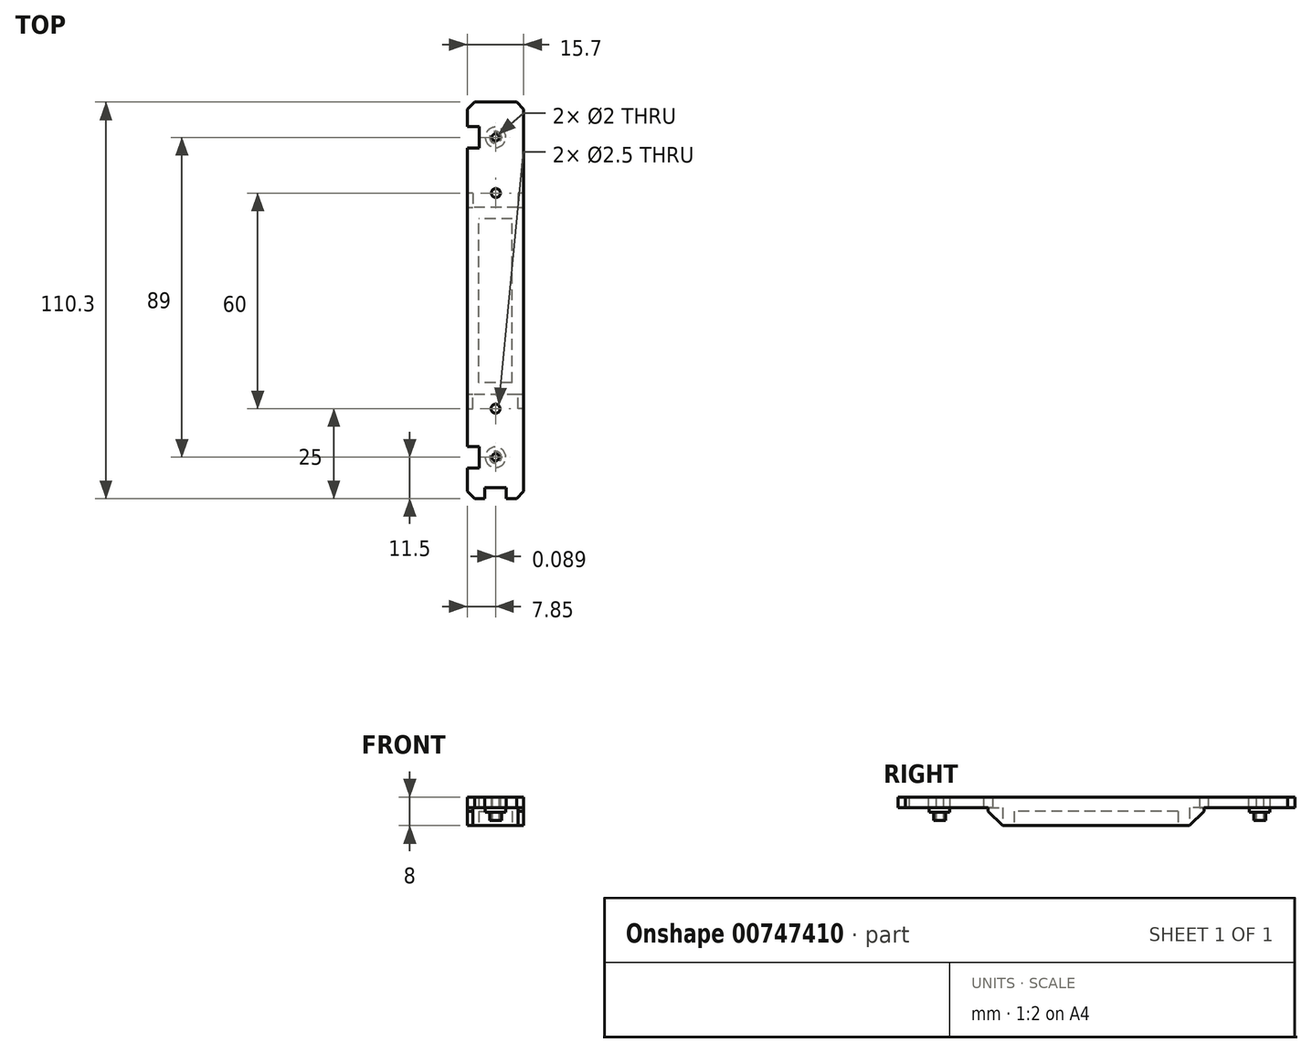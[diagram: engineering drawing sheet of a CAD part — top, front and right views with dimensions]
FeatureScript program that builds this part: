
annotation { "Feature Type Name" : "Feature", "Feature Type Description" : "" }
export const myFeature = defineFeature(function(context is Context, id is Id, definition is map)
    precondition{}
    {
        {
            var Q0;
            Q0=qCreatedBy(makeId("Right.planeOp"),FACE);
            var sketch = newSketch(context, id + "F0", { "sketchPlane" : qUnion([Q0])});
            skLineSegment(sketch, "E0", {"start": v(-25, 5) * mm, "end": v(0, 5) * mm});
            skLineSegment(sketch, "E1", {"start": v(0, 5) * mm, "end": v(0, 0) * mm});
            skLineSegment(sketch, "E2", {"start": v(60, 0) * mm, "end": v(60, 5) * mm});
            skLineSegment(sketch, "E3", {"start": v(60, 5) * mm, "end": v(85.3, 5) * mm});
            skLineSegment(sketch, "E4", {"start": v(85.3, 5) * mm, "end": v(85.3, 8) * mm});
            skLineSegment(sketch, "E5", {"start": v(-25, 8) * mm, "end": v(-25, 5) * mm});
            skLineSegment(sketch, "E6.trimOffspring", {"start": v(85.3, 8) * mm, "end": v(-25, 8) * mm});
            skLineSegment(sketch, "E7", {"start": v(0, 0) * mm, "end": v(0, 0) * mm});
            skLineSegment(sketch, "E8", {"start": v(0, 0) * mm, "end": v(60, 0) * mm});
            skSolve(sketch);
        }
        {
            var Q0;
            Q0 = qSketchRegion(id + "F0", true);
            extrude(context, id + "F1", {"entities" : qUnion([Q0]), "depth" : 15.7 * mm, "offsetDistance" : 25 * mm, "symmetric" : true});
        }
        {
            var Q0;
            Q0=makeQuery(id+"F1.opExtrude","CAP_EDGE",EDGE,{"disambiguationData":[OSD([sQuery(id+"F0.wireOp",EDGE,"E5")])],"isStart":false});
            var Q1;
            Q1=makeQuery(id+"F1.opExtrude","CAP_EDGE",EDGE,{"disambiguationData":[OSD([sQuery(id+"F0.wireOp",EDGE,"E5")])],"isStart":true});
            var Q2;
            Q2=makeQuery(id+"F1.opExtrude","CAP_EDGE",EDGE,{"disambiguationData":[OSD([sQuery(id+"F0.wireOp",EDGE,"E4")])],"isStart":false});
            var Q3;
            Q3=makeQuery(id+"F1.opExtrude","CAP_EDGE",EDGE,{"disambiguationData":[OSD([sQuery(id+"F0.wireOp",EDGE,"E4")])],"isStart":true});
            chamfer(context, id + "F2", {"entities" : qUnion([Q0, Q1, Q2, Q3]), "width" : 2 * mm, "tangentPropagation" : true});
        }
        {
            var Q0;
            Q0=makeQuery(id+"F1.opExtrude","SWEPT_FACE",FACE,{"disambiguationData":[OSD([sQuery(id+"F0.wireOp",EDGE,"E0")])]});
            var sketch = newSketch(context, id + "F3", { "sketchPlane" : qUnion([Q0])});
            skCircle(sketch, "E9", {"center": v(0, 13.5) * mm, "radius": 1 * mm});
            skCircle(sketch, "E10", {"center": v(0, -75.5) * mm, "radius": 1 * mm});
            skLineSegment(sketch, "E11", {"start": v(0, 13.5) * mm, "end": v(0, 0) * mm, "construction": true});
            skLineSegment(sketch, "E12", {"start": v(0, 0) * mm, "end": v(0, -75.5) * mm, "construction": true});
            skSolve(sketch);
        }
        {
            var Q0;
            Q0 = qSketchRegion(id + "F3", true);
            extrude(context, id + "F4", {"entities" : qUnion([Q0]), "operationType" : NewBodyOperationType.REMOVE, "endBound" : BoundingType.UP_TO_NEXT, "oppositeDirection" : true, "depth" : 25 * mm, "offsetDistance" : 25 * mm});
        }
        {
            var Q0;
            Q0=makeQuery(id+"F1.opExtrude","SWEPT_FACE",FACE,{"disambiguationData":[OSD([sQuery(id+"F0.wireOp",EDGE,"E7"),sQuery(id+"F0.wireOp",EDGE,"E8")])]});
            var sketch = newSketch(context, id + "F5", { "sketchPlane" : qUnion([Q0])});
            skLineSegment(sketch, "E13.bottom", {"start": v(6.25, 0) * mm, "end": v(-6.25, 0) * mm});
            skLineSegment(sketch, "E13.top", {"start": v(6.25, -4) * mm, "end": v(-6.25, -4) * mm});
            skLineSegment(sketch, "E13.left", {"start": v(6.25, 0) * mm, "end": v(6.25, -4) * mm});
            skLineSegment(sketch, "E13.right", {"start": v(-6.25, 0) * mm, "end": v(-6.25, -4) * mm});
            skLineSegment(sketch, "E14", {"start": v(0, -4) * mm, "end": v(0, 0) * mm, "construction": true});
            skPoint(sketch, "E14.startSnap0", {"position": v(0, -4) * mm});
            skLineSegment(sketch, "E15.bottom", {"start": v(6.25, -60) * mm, "end": v(-6.25, -60) * mm});
            skLineSegment(sketch, "E15.top", {"start": v(6.25, -56) * mm, "end": v(-6.25, -56) * mm});
            skLineSegment(sketch, "E15.left", {"start": v(6.25, -60) * mm, "end": v(6.25, -56) * mm});
            skLineSegment(sketch, "E15.right", {"start": v(-6.25, -60) * mm, "end": v(-6.25, -56) * mm});
            skSolve(sketch);
        }
        {
            var Q0;
            Q0 = qSketchRegion(id + "F5", true);
            var Q1;
            Q1=makeQuery(id+"F1.opExtrude","SWEPT_FACE",FACE,{"disambiguationData":[OSD([sQuery(id+"F0.wireOp",EDGE,"E0")])]});
            extrude(context, id + "F6", {"entities" : qUnion([Q0]), "operationType" : NewBodyOperationType.REMOVE, "endBound" : BoundingType.UP_TO_SURFACE, "oppositeDirection" : true, "depth" : 25 * mm, "endBoundEntityFace" : qUnion([Q1]), "offsetDistance" : 25 * mm});
        }
        {
            var Q0;
            {Q0=qUnion([makeQuery(id+"F6.boolean.opBoolean","MERGE",FACE,{"derivedFrom":[makeQuery(id+"F1.opExtrude","SWEPT_FACE",FACE,{"disambiguationData":[OSD([sQuery(id+"F0.wireOp",EDGE,"E0")])]})],"fromTools":[makeQuery(id+"F6.opExtrude","CAP_FACE",FACE,{"disambiguationData":[OSD([sQuery(id+"F5.wireOp",EDGE,"QtaLUQ9K-xFjA-aVn2-jr8E-2nqdviAdBmNi"),sQuery(id+"F5.wireOp",EDGE,"MIOGkYBv-3kq0-NffD-4QcD-ZkNMdwIdXdjM"),sQuery(id+"F5.wireOp",EDGE,"2ayCmlRU-f8e1-FQng-G2dl-z1bR76XOkfuW"),sQuery(id+"F5.wireOp",EDGE,"Q6Nk2F50-RIht-aVqs-q8m5-kIFtcKPUQnbz")])],"isStart":false})]}),makeQuery(id+"F6.boolean.opBoolean","MERGE",FACE,{"derivedFrom":[makeQuery(id+"F1.opExtrude","SWEPT_FACE",FACE,{"disambiguationData":[OSD([sQuery(id+"F0.wireOp",EDGE,"E3")])]})],"fromTools":[makeQuery(id+"F6.opExtrude","CAP_FACE",FACE,{"disambiguationData":[OSD([sQuery(id+"F5.wireOp",EDGE,"UIq0axqO-XxSW-t0FF-EL4X-YCJ9C5suXqDZ"),sQuery(id+"F5.wireOp",EDGE,"48w0VJL2-kqmk-4goN-fqhj-BqvBEsziLtPm"),sQuery(id+"F5.wireOp",EDGE,"iuIQCKwA-ER4D-4RKV-h3Pt-EvZXLoRTW6qv"),sQuery(id+"F5.wireOp",EDGE,"zWaE9cvL-vTQC-7oDd-e5Ol-owMjjvXLEkyw")])],"isStart":false})]})]);}
            var sketch = newSketch(context, id + "F7", { "sketchPlane" : qUnion([Q0])});
            skCircle(sketch, "E16", {"center": v(0, 0) * mm, "radius": 1.25 * mm});
            skCircle(sketch, "E17", {"center": v(0.09, -60) * mm, "radius": 1.25 * mm});
            skLineSegment(sketch, "E18", {"start": v(0, -4) * mm, "end": v(0, 0) * mm, "construction": true});
            skLineSegment(sketch, "E19", {"start": v(0.09, -60) * mm, "end": v(0, -56) * mm, "construction": true});
            skSolve(sketch);
        }
        {
            var Q0;
            Q0 = qSketchRegion(id + "F7", true);
            extrude(context, id + "F8", {"entities" : qUnion([Q0]), "operationType" : NewBodyOperationType.REMOVE, "endBound" : BoundingType.UP_TO_NEXT, "oppositeDirection" : true, "depth" : 25 * mm, "offsetDistance" : 25 * mm});
        }
        {
            var Q0;
            Q0=makeQuery(id+"F6.boolean.opBoolean","MERGE",FACE,{"derivedFrom":[makeQuery(id+"F1.opExtrude","SWEPT_FACE",FACE,{"disambiguationData":[OSD([sQuery(id+"F0.wireOp",EDGE,"E3")])]})],"fromTools":[makeQuery(id+"F6.opExtrude","CAP_FACE",FACE,{"disambiguationData":[OSD([sQuery(id+"F5.wireOp",EDGE,"UIq0axqO-XxSW-t0FF-EL4X-YCJ9C5suXqDZ"),sQuery(id+"F5.wireOp",EDGE,"48w0VJL2-kqmk-4goN-fqhj-BqvBEsziLtPm"),sQuery(id+"F5.wireOp",EDGE,"iuIQCKwA-ER4D-4RKV-h3Pt-EvZXLoRTW6qv")])],"isStart":false})]});
            var sketch = newSketch(context, id + "F9", { "sketchPlane" : qUnion([Q0])});
            skCircle(sketch, "E20", {"center": v(0, -75.5) * mm, "radius": 1.65 * mm});
            skCircle(sketch, "E21", {"center": v(0, 13.5) * mm, "radius": 1.65 * mm});
            skCircle(sketch, "E22.0", {"center": v(0, -75.5) * mm, "radius": 1 * mm});
            skCircle(sketch, "E23.0", {"center": v(0, 13.5) * mm, "radius": 1 * mm});
            skSolve(sketch);
        }
        {
            var Q0;
            Q0 = qSketchRegion(id + "F9", true);
            extrude(context, id + "F10", {"entities" : qUnion([Q0]), "operationType" : NewBodyOperationType.ADD, "depth" : 3.5 * mm, "offsetDistance" : 25 * mm});
        }
        {
            var Q0;
            Q0=makeQuery(id+"F1.opExtrude","SWEPT_FACE",FACE,{"disambiguationData":[OSD([sQuery(id+"F0.wireOp",EDGE,"E6.trimOffspring")])]});
            var sketch = newSketch(context, id + "F11", { "sketchPlane" : qUnion([Q0])});
            skLineSegment(sketch, "E24", {"start": v(-7.85, -10.5) * mm, "end": v(-4.5, -10.5) * mm});
            skLineSegment(sketch, "E25", {"start": v(-4.5, -10.5) * mm, "end": v(-4.5, -16.5) * mm});
            skLineSegment(sketch, "E26", {"start": v(-4.5, -16.5) * mm, "end": v(-7.85, -16.5) * mm});
            skLineSegment(sketch, "E27", {"start": v(-7.85, -16.5) * mm, "end": v(-7.85, -10.5) * mm});
            skLineSegment(sketch, "E28", {"start": v(0, -13.5) * mm, "end": v(0, -7.98) * mm, "construction": true});
            skLineSegment(sketch, "E29", {"start": v(0, -13.5) * mm, "end": v(-4.5, -13.5) * mm, "construction": true});
            skLineSegment(sketch, "E30.bottom", {"start": v(-7.85, 72.5) * mm, "end": v(-4.5, 72.5) * mm});
            skLineSegment(sketch, "E30.top", {"start": v(-7.85, 78.5) * mm, "end": v(-4.5, 78.5) * mm});
            skLineSegment(sketch, "E30.left", {"start": v(-7.85, 72.5) * mm, "end": v(-7.85, 78.5) * mm});
            skLineSegment(sketch, "E30.right", {"start": v(-4.5, 72.5) * mm, "end": v(-4.5, 78.5) * mm});
            skLineSegment(sketch, "E31", {"start": v(-4.5, 75.5) * mm, "end": v(0, 75.5) * mm, "construction": true});
            skSolve(sketch);
        }
        {
            var Q0;
            Q0 = qSketchRegion(id + "F11", true);
            extrude(context, id + "F12", {"entities" : qUnion([Q0]), "operationType" : NewBodyOperationType.REMOVE, "endBound" : BoundingType.UP_TO_NEXT, "oppositeDirection" : true, "depth" : 25 * mm, "offsetDistance" : 25 * mm});
        }
        {
            var Q0;
            Q0=makeQuery(id+"F6.boolean.opBoolean","MERGE",FACE,{"derivedFrom":[makeQuery(id+"F1.opExtrude","SWEPT_FACE",FACE,{"disambiguationData":[OSD([sQuery(id+"F0.wireOp",EDGE,"E3")])]})],"fromTools":[makeQuery(id+"F6.opExtrude","CAP_FACE",FACE,{"disambiguationData":[OSD([sQuery(id+"F5.wireOp",EDGE,"UIq0axqO-XxSW-t0FF-EL4X-YCJ9C5suXqDZ"),sQuery(id+"F5.wireOp",EDGE,"48w0VJL2-kqmk-4goN-fqhj-BqvBEsziLtPm"),sQuery(id+"F5.wireOp",EDGE,"iuIQCKwA-ER4D-4RKV-h3Pt-EvZXLoRTW6qv")])],"isStart":false})]});
            var sketch = newSketch(context, id + "F13", { "sketchPlane" : qUnion([Q0])});
            skCircle(sketch, "E32", {"center": v(0, -75.5) * mm, "radius": 2.85 * mm});
            skCircle(sketch, "E33", {"center": v(0, 13.5) * mm, "radius": 2.85 * mm});
            skCircle(sketch, "E34.0", {"center": v(0, 13.5) * mm, "radius": 1 * mm});
            skCircle(sketch, "E34.1", {"center": v(0, -75.5) * mm, "radius": 1 * mm});
            skSolve(sketch);
        }
        {
            var Q0;
            Q0 = qSketchRegion(id + "F13", true);
            extrude(context, id + "F14", {"entities" : qUnion([Q0]), "operationType" : NewBodyOperationType.ADD, "depth" : 1.2 * mm, "offsetDistance" : 25 * mm});
        }
        {
            var Q0;
            Q0=makeQuery(id+"F6.boolean.opBoolean","MERGE",FACE,{"derivedFrom":[makeQuery(id+"F1.opExtrude","SWEPT_FACE",FACE,{"disambiguationData":[OSD([sQuery(id+"F0.wireOp",EDGE,"E0")])]})],"fromTools":[makeQuery(id+"F6.opExtrude","CAP_FACE",FACE,{"disambiguationData":[OSD([sQuery(id+"F5.wireOp",EDGE,"QtaLUQ9K-xFjA-aVn2-jr8E-2nqdviAdBmNi"),sQuery(id+"F5.wireOp",EDGE,"MIOGkYBv-3kq0-NffD-4QcD-ZkNMdwIdXdjM"),sQuery(id+"F5.wireOp",EDGE,"2ayCmlRU-f8e1-FQng-G2dl-z1bR76XOkfuW")])],"isStart":false})]});
            var sketch = newSketch(context, id + "F15", { "sketchPlane" : qUnion([Q0])});
            skLineSegment(sketch, "E35.bottom", {"start": v(3, 25) * mm, "end": v(-3, 25) * mm});
            skLineSegment(sketch, "E35.top", {"start": v(3, 22) * mm, "end": v(-3, 22) * mm});
            skLineSegment(sketch, "E35.left", {"start": v(3, 25) * mm, "end": v(3, 22) * mm});
            skLineSegment(sketch, "E35.right", {"start": v(-3, 25) * mm, "end": v(-3, 22) * mm});
            skLineSegment(sketch, "E36", {"start": v(0, 22) * mm, "end": v(0, 13.5) * mm, "construction": true});
            skSolve(sketch);
        }
        {
            var Q0;
            Q0 = qSketchRegion(id + "F15", true);
            extrude(context, id + "F16", {"entities" : qUnion([Q0]), "operationType" : NewBodyOperationType.REMOVE, "endBound" : BoundingType.UP_TO_NEXT, "oppositeDirection" : true, "depth" : 25 * mm, "offsetDistance" : 25 * mm});
        }
        {
            var Q0;
            Q0=makeQuery(id+"F1.opExtrude","SWEPT_FACE",FACE,{"disambiguationData":[OSD([sQuery(id+"F0.wireOp",EDGE,"E8")])]});
            var sketch = newSketch(context, id + "F17", { "sketchPlane" : qUnion([Q0])});
            skLineSegment(sketch, "E37.bottom", {"start": v(4.65, -7.2) * mm, "end": v(-4.65, -7.2) * mm});
            skLineSegment(sketch, "E37.top", {"start": v(4.65, -52.8) * mm, "end": v(-4.65, -52.8) * mm});
            skLineSegment(sketch, "E37.left", {"start": v(4.65, -7.2) * mm, "end": v(4.65, -52.8) * mm});
            skLineSegment(sketch, "E37.right", {"start": v(-4.65, -7.2) * mm, "end": v(-4.65, -52.8) * mm});
            skLineSegment(sketch, "E38", {"start": v(4.65, -30) * mm, "end": v(7.85, -30) * mm, "construction": true});
            skLineSegment(sketch, "E39", {"start": v(-4.65, -30) * mm, "end": v(-7.85, -30) * mm, "construction": true});
            skSolve(sketch);
        }
        {
            var Q0;
            Q0 = qSketchRegion(id + "F17", true);
            var Q1;
            Q1=makeQuery(id+"F1.opExtrude","SWEPT_FACE",FACE,{"disambiguationData":[OSD([sQuery(id+"F0.wireOp",EDGE,"E6.trimOffspring")])]});
            extrude(context, id + "F18", {"entities" : qUnion([Q0]), "operationType" : NewBodyOperationType.REMOVE, "endBound" : BoundingType.UP_TO_SURFACE, "oppositeDirection" : true, "depth" : 25 * mm, "endBoundEntityFace" : qUnion([Q1]), "hasOffset" : true, "offsetDistance" : 4 * mm});
        }
        {
            var Q0;
            {var subQ0=sQuery(id+"F0.wireOp",EDGE,"E8");var subQ1=sQuery(id+"F0.wireOp",EDGE,"E1");Q0=makeQuery(id+"F6.boolean.opBoolean","SPLIT",EDGE,{"disambiguationData":[TD([makeQuery(id+"F6.opExtrude","SWEPT_FACE",FACE,{"disambiguationData":[OSD([sQuery(id+"F5.wireOp",EDGE,"E13.right")])]})])],"derivedFrom":makeQuery(id+"F1.opExtrude","SWEPT_EDGE",EDGE,{"disambiguationData":[OSD([subQ1,subQ0])]})});}
            var Q1;
            {var subQ0=sQuery(id+"F0.wireOp",EDGE,"E8");var subQ1=sQuery(id+"F0.wireOp",EDGE,"E1");Q1=makeQuery(id+"F6.boolean.opBoolean","SPLIT",EDGE,{"disambiguationData":[TD([makeQuery(id+"F6.opExtrude","SWEPT_FACE",FACE,{"disambiguationData":[OSD([sQuery(id+"F5.wireOp",EDGE,"E13.left")])]})])],"derivedFrom":makeQuery(id+"F1.opExtrude","SWEPT_EDGE",EDGE,{"disambiguationData":[OSD([subQ1,subQ0])]})});}
            var Q2;
            {var subQ0=sQuery(id+"F0.wireOp",EDGE,"E8");var subQ1=sQuery(id+"F0.wireOp",EDGE,"E2");Q2=makeQuery(id+"F6.boolean.opBoolean","SPLIT",EDGE,{"disambiguationData":[TD([makeQuery(id+"F6.opExtrude","SWEPT_FACE",FACE,{"disambiguationData":[OSD([sQuery(id+"F5.wireOp",EDGE,"E15.right")])]})])],"derivedFrom":makeQuery(id+"F1.opExtrude","SWEPT_EDGE",EDGE,{"disambiguationData":[OSD([subQ1,subQ0])]})});}
            var Q3;
            {var subQ0=sQuery(id+"F0.wireOp",EDGE,"E8");var subQ1=sQuery(id+"F0.wireOp",EDGE,"E2");Q3=makeQuery(id+"F6.boolean.opBoolean","SPLIT",EDGE,{"disambiguationData":[TD([makeQuery(id+"F6.opExtrude","SWEPT_FACE",FACE,{"disambiguationData":[OSD([sQuery(id+"F5.wireOp",EDGE,"E15.left")])]})])],"derivedFrom":makeQuery(id+"F1.opExtrude","SWEPT_EDGE",EDGE,{"disambiguationData":[OSD([subQ1,subQ0])]})});}
            chamfer(context, id + "F19", {"entities" : qUnion([Q0, Q1, Q2, Q3]), "width" : 4 * mm, "tangentPropagation" : true});
        }
    });
